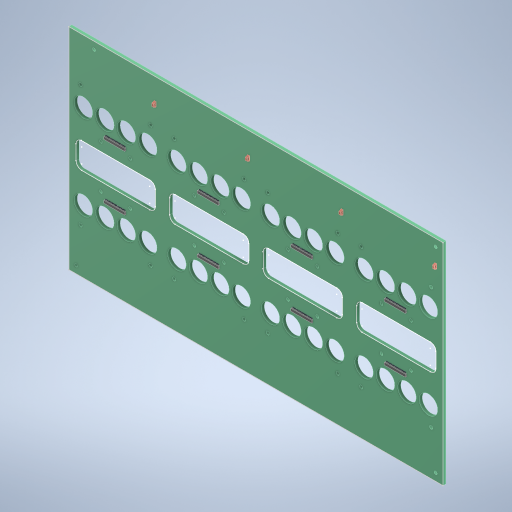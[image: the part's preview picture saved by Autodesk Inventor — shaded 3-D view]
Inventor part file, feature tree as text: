
AUTODESK INVENTOR PART (.ipt)
format: ipt  version: 2023 (Build 270158000, 158)  size: 2,089,472 bytes
history: native  units: in
note: dims shown in document units (in); Inventor stores cm internally (conversion verified against a paired STEP export)
features: sketch x6, hole x2, other x1
ambient origin geometry x8: Origin, YZ Plane, XZ Plane, XY Plane, X Axis, Y Axis, Z Axis, Center Point
bodies: Solid1 (feature_tree), Solid2 (feature_tree), Solid3 (feature_tree), Solid4 (feature_tree), Solid5 (feature_tree), Solid6 (feature_tree), Solid7 (feature_tree), Solid8 (feature_tree), Solid9 (feature_tree), Solid10 (feature_tree), Solid11 (feature_tree), Solid12 (feature_tree), Solid13 (feature_tree), Solid14 (feature_tree), Solid15 (feature_tree), Solid16 (feature_tree), Solid17 (feature_tree), Solid18 (feature_tree), Solid19 (feature_tree), Solid20 (feature_tree), Solid21 (feature_tree), Solid22 (feature_tree), Solid23 (feature_tree), Solid24 (feature_tree), Solid25 (feature_tree), Solid26 (feature_tree), Solid27 (feature_tree), Solid28 (feature_tree), Solid29 (feature_tree), Solid30 (feature_tree), Solid31 (feature_tree), Solid32 (feature_tree), Solid33 (feature_tree), Solid34 (feature_tree), Solid35 (feature_tree), Solid36 (feature_tree), Solid37 (feature_tree), Solid38 (feature_tree), Solid39 (feature_tree), Solid40 (feature_tree), Solid41 (feature_tree), Solid42 (feature_tree), Solid43 (feature_tree), Solid44 (feature_tree), Solid45 (feature_tree), Solid46 (feature_tree), Solid47 (feature_tree), Solid48 (feature_tree), Solid49 (feature_tree), Solid50 (feature_tree), Solid51 (feature_tree), Solid52 (feature_tree), Solid53 (feature_tree), Solid54 (feature_tree), Solid55 (feature_tree), Solid56 (feature_tree), Solid57 (feature_tree), Solid58 (feature_tree), Solid59 (feature_tree), Solid60 (feature_tree), Solid61 (feature_tree), Solid62 (feature_tree), Solid63 (feature_tree), Solid64 (feature_tree), Solid65 (feature_tree), Solid66 (feature_tree), Solid67 (feature_tree), Solid68 (feature_tree), Solid69 (feature_tree), Solid70 (feature_tree), Solid71 (feature_tree), Solid72 (feature_tree), Solid73 (feature_tree), Solid74 (feature_tree), Solid75 (feature_tree), Solid76 (feature_tree), Solid77 (feature_tree), Solid78 (feature_tree), Solid79 (feature_tree), Solid80 (feature_tree), Solid81 (feature_tree), Solid82 (feature_tree), Solid83 (feature_tree), Solid84 (feature_tree), Solid85 (feature_tree), Solid86 (feature_tree), Solid87 (feature_tree), Solid88 (feature_tree), Solid89 (feature_tree), Solid90 (feature_tree), Solid91 (feature_tree), Solid92 (feature_tree), Solid93 (feature_tree), Solid94 (feature_tree), Solid95 (feature_tree), Solid96 (feature_tree), Solid97 (feature_tree), Solid98 (feature_tree), Solid99 (feature_tree), Solid100 (feature_tree), Solid101 (feature_tree), Solid102 (feature_tree), Solid103 (feature_tree), Solid104 (feature_tree), Solid105 (feature_tree), Solid106 (feature_tree), Solid107 (feature_tree), Solid108 (feature_tree), Solid109 (feature_tree), Solid110 (feature_tree), Solid111 (feature_tree), Solid112 (feature_tree), Solid113 (feature_tree), Solid114 (feature_tree), Solid115 (feature_tree), Solid116 (feature_tree), Solid117 (feature_tree), Solid118 (feature_tree), Solid119 (feature_tree), Solid120 (feature_tree), Solid121 (feature_tree), Solid122 (feature_tree), Solid123 (feature_tree), Solid124 (feature_tree), Solid125 (feature_tree), Solid126 (feature_tree), Solid127 (feature_tree), Solid128 (feature_tree), Solid129 (feature_tree), Solid130 (feature_tree), Solid131 (feature_tree), Solid132 (feature_tree), Solid133 (feature_tree), Solid134 (feature_tree), Solid135 (feature_tree), Solid136 (feature_tree), Solid137 (feature_tree), Solid138 (feature_tree), Solid139 (feature_tree), Solid140 (feature_tree), Solid141 (feature_tree), Solid142 (feature_tree), Solid143 (feature_tree), Solid144 (feature_tree), Solid145 (feature_tree), Solid146 (feature_tree), Solid147 (feature_tree), Solid148 (feature_tree), Solid149 (feature_tree), Solid150 (feature_tree), Solid151 (feature_tree), Solid152 (feature_tree), Solid153 (feature_tree), Solid154 (feature_tree), Solid155 (feature_tree), Solid156 (feature_tree), Solid157 (feature_tree), Solid158 (feature_tree), Solid159 (feature_tree), Solid160 (feature_tree), Solid161 (feature_tree), Solid162 (feature_tree), Solid163 (feature_tree), Solid164 (feature_tree), Solid165 (feature_tree), Solid166 (feature_tree), Solid167 (feature_tree), Solid168 (feature_tree), Solid169 (feature_tree), Solid170 (feature_tree), Solid171 (feature_tree), Solid172 (feature_tree), Solid173 (feature_tree), Solid174 (feature_tree), Solid175 (feature_tree), Solid176 (feature_tree), Solid177 (feature_tree), Solid178 (feature_tree), Solid179 (feature_tree), Solid180 (feature_tree), Solid181 (feature_tree), Solid182 (feature_tree), Solid183 (feature_tree), Solid184 (feature_tree), Solid185 (feature_tree), Solid186 (feature_tree), Solid187 (feature_tree), Solid188 (feature_tree), Solid189 (feature_tree), Solid190 (feature_tree), Solid191 (feature_tree), Solid192 (feature_tree), Solid193 (feature_tree), Solid194 (feature_tree), Solid195 (feature_tree), Solid196 (feature_tree), Solid197 (feature_tree), Solid198 (feature_tree), Solid199 (feature_tree), Solid200 (feature_tree), Solid201 (feature_tree), Solid202 (feature_tree), Solid203 (feature_tree), Solid204 (feature_tree), Solid205 (feature_tree), Solid206 (feature_tree), Solid207 (feature_tree), Solid208 (feature_tree), Solid209 (feature_tree), Solid210 (feature_tree), Solid211 (feature_tree), Solid212 (feature_tree), Solid213 (feature_tree), Solid214 (feature_tree), Solid215 (feature_tree), Solid216 (feature_tree), Solid217 (feature_tree), Solid218 (feature_tree), Solid219 (feature_tree), Solid220 (feature_tree), Solid221 (feature_tree), Solid222 (feature_tree), Solid223 (feature_tree), Solid224 (feature_tree), Solid225 (feature_tree), Solid226 (feature_tree), Solid227 (feature_tree), Solid228 (feature_tree), Solid229 (feature_tree), Solid230 (feature_tree), Solid231 (feature_tree), Solid232 (feature_tree), Solid233 (feature_tree), Solid234 (feature_tree), Solid235 (feature_tree), Solid236 (feature_tree), Solid237 (feature_tree), Solid238 (feature_tree), Solid239 (feature_tree), Solid240 (feature_tree), Solid241 (feature_tree), Solid242 (feature_tree), Solid243 (feature_tree), Solid244 (feature_tree), Solid245 (feature_tree), Solid246 (feature_tree), Solid247 (feature_tree), Solid248 (feature_tree), Solid249 (feature_tree), Solid250 (feature_tree), Solid251 (feature_tree), Solid252 (feature_tree), Solid253 (feature_tree), Solid254 (feature_tree), Solid255 (feature_tree), Solid256 (feature_tree), Solid257 (feature_tree), Solid258 (feature_tree), Solid259 (feature_tree), Solid260 (feature_tree), Solid261 (feature_tree), Solid262 (feature_tree), Solid263 (feature_tree), Solid264 (feature_tree), Solid265 (feature_tree), Solid266 (feature_tree), Solid267 (feature_tree), Solid268 (feature_tree), Solid269 (feature_tree), Solid270 (feature_tree), Solid271 (feature_tree), Solid272 (feature_tree), Solid273 (feature_tree), Solid274 (feature_tree), Solid275 (feature_tree), Solid276 (feature_tree), Solid277 (feature_tree), Solid278 (feature_tree), Solid279 (feature_tree), Solid280 (feature_tree), Solid281 (feature_tree), Solid282 (feature_tree), Solid283 (feature_tree), Solid284 (feature_tree), Solid285 (feature_tree), Solid286 (feature_tree), Solid287 (feature_tree), Solid288 (feature_tree), Solid289 (feature_tree), Solid290 (feature_tree), Solid291 (feature_tree), Solid292 (feature_tree), Solid293 (feature_tree), Solid294 (feature_tree), Solid295 (feature_tree), Solid296 (feature_tree), Solid297 (feature_tree), Solid298 (feature_tree), Solid299 (feature_tree), Solid300 (feature_tree), Solid301 (feature_tree), Solid302 (feature_tree), Solid303 (feature_tree), Solid304 (feature_tree), Solid305 (feature_tree), Solid306 (feature_tree), Solid307 (feature_tree), Solid308 (feature_tree), Solid309 (feature_tree), Solid310 (feature_tree), Solid311 (feature_tree), Solid312 (feature_tree), Solid313 (feature_tree), Solid314 (feature_tree), Solid315 (feature_tree), Solid316 (feature_tree), Solid317 (feature_tree), Solid318 (feature_tree), Solid319 (feature_tree), Solid320 (feature_tree), Solid321 (feature_tree), Solid322 (feature_tree), Solid323 (feature_tree), Solid324 (feature_tree), Solid325 (feature_tree), Solid326 (feature_tree), Solid327 (feature_tree), Solid328 (feature_tree), Solid329 (feature_tree), Solid330 (feature_tree), Solid331 (feature_tree), Solid332 (feature_tree), Solid333 (feature_tree), Solid334 (feature_tree), Solid335 (feature_tree), Solid336 (feature_tree), Solid337 (feature_tree), Solid338 (feature_tree), Solid339 (feature_tree), Solid340 (feature_tree), Solid341 (feature_tree), Solid342 (feature_tree), Solid343 (feature_tree), Solid344 (feature_tree), Solid345 (feature_tree), Solid346 (feature_tree), Solid347 (feature_tree), Solid348 (feature_tree), Solid349 (feature_tree), Solid350 (feature_tree), Solid351 (feature_tree), Solid352 (feature_tree), Solid353 (feature_tree), Solid354 (feature_tree), Solid355 (feature_tree), Solid356 (feature_tree), Solid357 (feature_tree), Solid358 (feature_tree), Solid359 (feature_tree), Solid360 (feature_tree), Solid361 (feature_tree), Solid362 (feature_tree), Solid363 (feature_tree), Solid364 (feature_tree), Solid365 (feature_tree), Solid366 (feature_tree), Solid367 (feature_tree), Solid368 (feature_tree), Solid369 (feature_tree), Solid370 (feature_tree), Solid371 (feature_tree), Solid372 (feature_tree), Solid373 (feature_tree), Solid374 (feature_tree), Solid375 (feature_tree), Solid376 (feature_tree), Solid377 (feature_tree), Solid378 (feature_tree), Solid379 (feature_tree), Solid380 (feature_tree), Solid381 (feature_tree), Solid382 (feature_tree), Solid383 (feature_tree), Solid384 (feature_tree), Solid385 (feature_tree), Solid386 (feature_tree), Solid387 (feature_tree), Solid388 (feature_tree), Solid389 (feature_tree), Solid390 (feature_tree), Solid391 (feature_tree), Solid392 (feature_tree), Solid393 (feature_tree), Solid394 (feature_tree), Solid395 (feature_tree), Solid396 (feature_tree), Solid397 (feature_tree), Solid398 (feature_tree), Solid399 (feature_tree), Solid400 (feature_tree), Solid401 (feature_tree), Solid402 (feature_tree), Solid403 (feature_tree), Solid404 (feature_tree), Solid405 (feature_tree), Solid406 (feature_tree), Solid407 (feature_tree), Solid408 (feature_tree), Solid409 (feature_tree), Solid410 (feature_tree), Solid411 (feature_tree), Solid412 (feature_tree), Solid413 (feature_tree), Solid414 (feature_tree), Solid415 (feature_tree), Solid416 (feature_tree), Solid417 (feature_tree), Solid418 (feature_tree), Solid419 (feature_tree), Solid420 (feature_tree), Solid421 (feature_tree), Solid422 (feature_tree), Solid423 (feature_tree), Solid424 (feature_tree), Solid425 (feature_tree), Solid426 (feature_tree), Solid427 (feature_tree), Solid428 (feature_tree), Solid429 (feature_tree), Solid430 (feature_tree), Solid431 (feature_tree), Solid432 (feature_tree), Solid433 (feature_tree), Solid434 (feature_tree), Solid435 (feature_tree), Solid436 (feature_tree), Solid437 (feature_tree), Solid438 (feature_tree), Solid439 (feature_tree), Solid440 (feature_tree), Solid441 (feature_tree), Solid442 (feature_tree), Solid443 (feature_tree), Solid444 (feature_tree), Solid445 (feature_tree)
feature tree (9):
  other  "Repaired Geometry1"
  sketch  "3D Sketch1"
  sketch  "3D Sketch2"
  sketch  "3D Sketch3"
  sketch  "3D Sketch4"
  sketch  "Sketch1"  dims[d23=4.5in d24=2.25in d25=0.4593in d27=0.4593in d30=0.3937in d31=0.2362in d32=0.1575in d33=0.0787in d34=90.0deg d35=0.315in d36=0.8108in d37=1.6929in d38=0.8465in d40=0.9055in d41=0.2297in d42=0.2297in d43=1.2992in d44=0.748in d45=1.4961in d46=1.2992in d47=0.07in d48=0.2362in d49=0.119in d50=0.0787in d51=0.5635in d52=0.315in d53=0.8108in d54=1.5748in d56=2.0in d57=0.3937in d59=0.3937in]
  hole  "Hole1"  [1 undecoded]
  hole  "Hole2"  [1 undecoded]
  sketch  "3D Sketch5"
note: 2 required parameter values undecoded (feature->parameter linkage not recoverable at this tier; creation-order binding heuristic only, values carry confidence <= 0.55)
